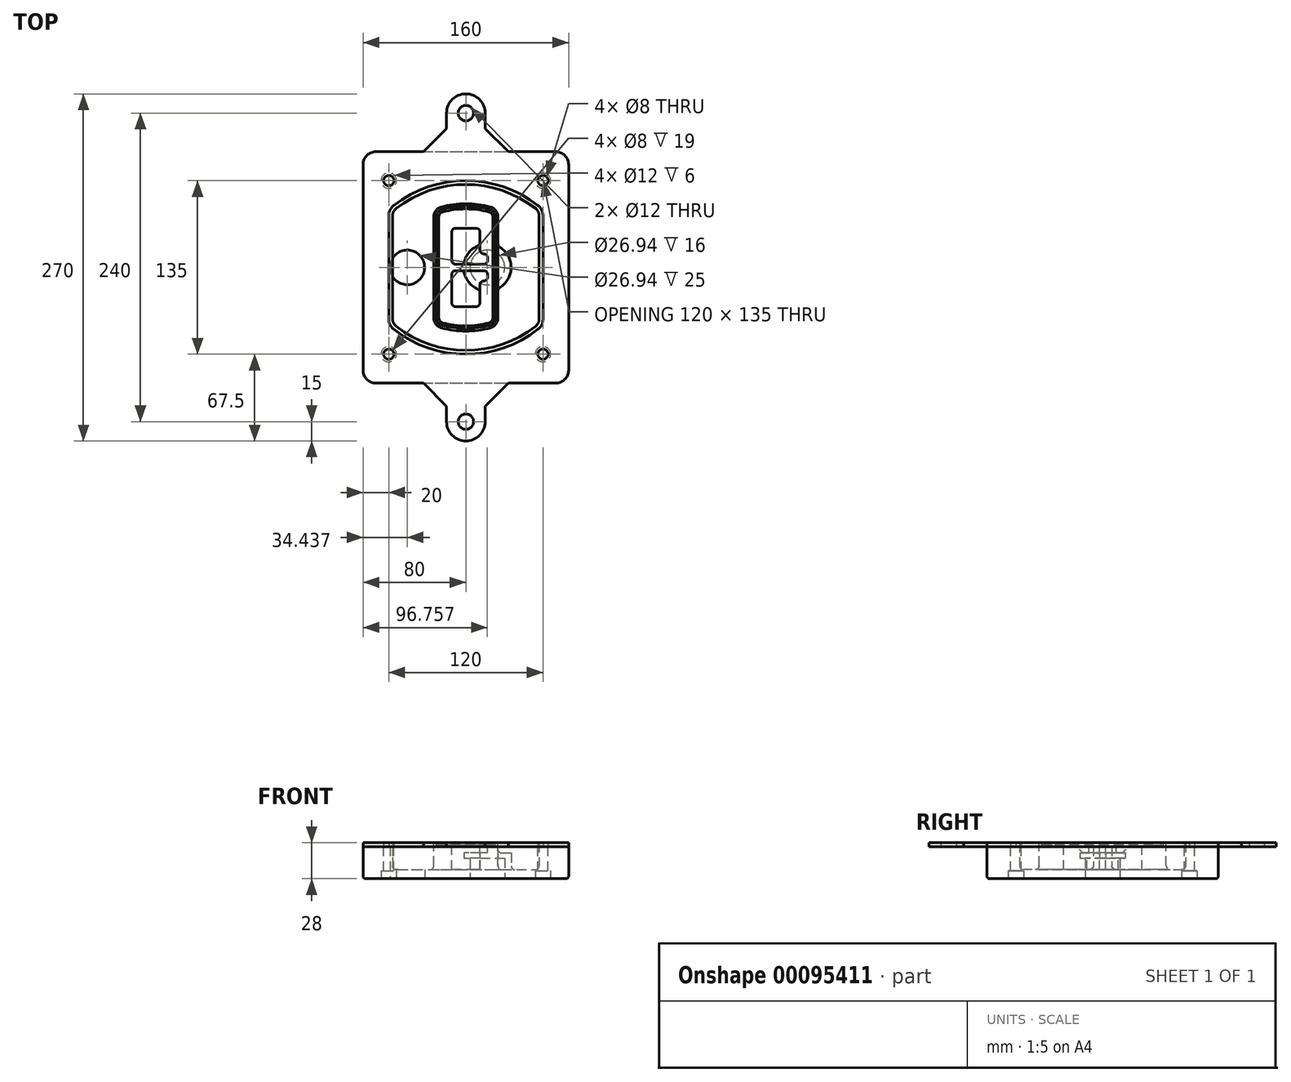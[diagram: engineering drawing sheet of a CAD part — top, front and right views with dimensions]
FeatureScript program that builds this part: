
annotation { "Feature Type Name" : "Feature", "Feature Type Description" : "" }
export const myFeature = defineFeature(function(context is Context, id is Id, definition is map)
    precondition{}
    {
        {
            var Q0;
            Q0=qCreatedBy(makeId("Top.planeOp"),FACE);
            var sketch = newSketch(context, id + "F0", { "sketchPlane" : qUnion([Q0])});
            skPoint(sketch, "E0.rect.middle", {"position": v(0, 0) * mm});
            skLineSegment(sketch, "E1.bottom", {"start": v(-70, -90) * mm, "end": v(70, -90) * mm});
            skLineSegment(sketch, "E1.top", {"start": v(-70, 90) * mm, "end": v(70, 90) * mm});
            skLineSegment(sketch, "E1.left", {"start": v(-80, -80) * mm, "end": v(-80, 80) * mm});
            skLineSegment(sketch, "E1.right", {"start": v(80, -80) * mm, "end": v(80, 80) * mm});
            skLineSegment(sketch, "E2", {"start": v(-80, 90) * mm, "end": v(80, -90) * mm, "construction": true});
            skLineSegment(sketch, "E3", {"start": v(80, 90) * mm, "end": v(-80, -90) * mm, "construction": true});
            skCircle(sketch, "E4", {"center": v(-60, 67.5) * mm, "radius": 4 * mm});
            skCircle(sketch, "E5", {"center": v(60, 67.5) * mm, "radius": 4 * mm});
            skCircle(sketch, "E6", {"center": v(60, -67.5) * mm, "radius": 4 * mm});
            skCircle(sketch, "E7", {"center": v(-60, -67.5) * mm, "radius": 4 * mm});
            skLineSegment(sketch, "E8", {"start": v(-60, 67.5) * mm, "end": v(60, 67.5) * mm, "construction": true});
            skLineSegment(sketch, "E9", {"start": v(60, 67.5) * mm, "end": v(60, -67.5) * mm, "construction": true});
            skLineSegment(sketch, "E10", {"start": v(60, -67.5) * mm, "end": v(-60, -67.5) * mm, "construction": true});
            skLineSegment(sketch, "E11", {"start": v(-60, -67.5) * mm, "end": v(-60, 67.5) * mm, "construction": true});
            skLineSegment(sketch, "E12", {"start": v(-60, 40.3) * mm, "end": v(-60, -40.3) * mm});
            skLineSegment(sketch, "E13", {"start": v(60, 40.3) * mm, "end": v(60, -40.3) * mm});
            skArc(sketch, "E14", {"start": v(56.15, 48.18) * mm, "mid": v(0, 67.5) * mm, "end": v(-56.15, 48.18) * mm});
            skArc(sketch, "E15", {"start": v(-56.15, -48.18) * mm, "mid": v(0, -67.5) * mm, "end": v(56.15, -48.18) * mm});
            skLineSegment(sketch, "E16", {"start": v(-60, 0) * mm, "end": v(60, 0) * mm, "construction": true});
            skPoint(sketch, "E17.visualSharp", {"position": v(-60, -45) * mm});
            skArc(sketch, "E17.filletArc", {"start": v(-60, -40.3) * mm, "mid": v(-58.99, -44.68) * mm, "end": v(-56.15, -48.18) * mm});
            skPoint(sketch, "E18.visualSharp", {"position": v(-60, 45) * mm});
            skArc(sketch, "E18.filletArc", {"start": v(-56.15, 48.18) * mm, "mid": v(-58.99, 44.68) * mm, "end": v(-60, 40.3) * mm});
            skPoint(sketch, "E19.visualSharp", {"position": v(60, 45) * mm});
            skArc(sketch, "E19.filletArc", {"start": v(60, 40.3) * mm, "mid": v(58.99, 44.68) * mm, "end": v(56.15, 48.18) * mm});
            skPoint(sketch, "E20.visualSharp", {"position": v(60, -45) * mm});
            skArc(sketch, "E20.filletArc", {"start": v(56.15, -48.18) * mm, "mid": v(58.99, -44.68) * mm, "end": v(60, -40.3) * mm});
            skPoint(sketch, "E21.visualSharp", {"position": v(-80, 90) * mm});
            skArc(sketch, "E21.filletArc", {"start": v(-70, 90) * mm, "mid": v(-77.07, 87.07) * mm, "end": v(-80, 80) * mm});
            skPoint(sketch, "E22.visualSharp", {"position": v(80, 90) * mm});
            skArc(sketch, "E22.filletArc", {"start": v(80, 80) * mm, "mid": v(77.07, 87.07) * mm, "end": v(70, 90) * mm});
            skPoint(sketch, "E23.visualSharp", {"position": v(80, -90) * mm});
            skArc(sketch, "E23.filletArc", {"start": v(70, -90) * mm, "mid": v(77.07, -87.07) * mm, "end": v(80, -80) * mm});
            skPoint(sketch, "E24.visualSharp", {"position": v(-80, -90) * mm});
            skArc(sketch, "E24.filletArc", {"start": v(-80, -80) * mm, "mid": v(-77.07, -87.07) * mm, "end": v(-70, -90) * mm});
            skArc(sketch, "E25.0", {"start": v(57, 40.3) * mm, "mid": v(56.3, 43.36) * mm, "end": v(54.3, 45.81) * mm});
            skLineSegment(sketch, "E25.1", {"start": v(57, 40.3) * mm, "end": v(57, -40.3) * mm});
            skArc(sketch, "E25.2", {"start": v(54.3, -45.81) * mm, "mid": v(56.3, -43.36) * mm, "end": v(57, -40.3) * mm});
            skArc(sketch, "E25.3", {"start": v(-54.3, -45.81) * mm, "mid": v(0, -64.5) * mm, "end": v(54.3, -45.81) * mm});
            skArc(sketch, "E25.4", {"start": v(-57, -40.3) * mm, "mid": v(-56.3, -43.36) * mm, "end": v(-54.3, -45.81) * mm});
            skArc(sketch, "E25.5", {"start": v(54.3, 45.81) * mm, "mid": v(0, 64.5) * mm, "end": v(-54.3, 45.81) * mm});
            skLineSegment(sketch, "E25.6", {"start": v(-57, 40.3) * mm, "end": v(-57, -40.3) * mm});
            skArc(sketch, "E25.7", {"start": v(-54.3, 45.81) * mm, "mid": v(-56.3, 43.36) * mm, "end": v(-57, 40.3) * mm});
            skArc(sketch, "E26.0", {"start": v(-58.62, 51.33) * mm, "mid": v(-62.58, 46.43) * mm, "end": v(-64, 40.3) * mm});
            skArc(sketch, "E26.1", {"start": v(58.62, 51.33) * mm, "mid": v(0, 71.5) * mm, "end": v(-58.62, 51.33) * mm});
            skArc(sketch, "E26.2", {"start": v(64, 40.3) * mm, "mid": v(62.58, 46.43) * mm, "end": v(58.62, 51.33) * mm});
            skLineSegment(sketch, "E26.3", {"start": v(64, 40.3) * mm, "end": v(64, -40.3) * mm});
            skArc(sketch, "E26.4", {"start": v(58.62, -51.33) * mm, "mid": v(62.58, -46.43) * mm, "end": v(64, -40.3) * mm});
            skLineSegment(sketch, "E26.5", {"start": v(-64, 40.3) * mm, "end": v(-64, -40.3) * mm});
            skArc(sketch, "E26.6", {"start": v(-58.62, -51.33) * mm, "mid": v(0, -71.5) * mm, "end": v(58.62, -51.33) * mm});
            skArc(sketch, "E26.7", {"start": v(-64, -40.3) * mm, "mid": v(-62.58, -46.43) * mm, "end": v(-58.62, -51.33) * mm});
            skSolve(sketch);
        }
        {
            var Q0;
            Q0=makeQuery(id+"F0.imprint","IMPRINT",FACE,{"disambiguationData":[TD([[makeQuery(id+"F0.imprint","IMPRINT",EDGE,{"derivedFrom":sQuery(id+"F0.wireOp",EDGE,"E1.bottom")}),1.0]])]});
            var Q1;
            Q1=makeQuery(id+"F0.imprint","IMPRINT",FACE,{"disambiguationData":[TD([[makeQuery(id+"F0.imprint","IMPRINT",EDGE,{"derivedFrom":sQuery(id+"F0.wireOp",EDGE,"E12")}),1.0]])]});
            var Q2;
            Q2=makeQuery(id+"F0.imprint","IMPRINT",FACE,{"disambiguationData":[TD([[makeQuery(id+"F0.imprint","IMPRINT",EDGE,{"derivedFrom":sQuery(id+"F0.wireOp",EDGE,"E25.0")}),1.0]])]});
            var Q3;
            Q3=makeQuery(id+"F0.imprint","IMPRINT",FACE,{"disambiguationData":[TD([[makeQuery(id+"F0.imprint","IMPRINT",EDGE,{"derivedFrom":sQuery(id+"F0.wireOp",EDGE,"E12")}),-1.0]])]});
            extrude(context, id + "F1", {"entities" : qUnion([Q0, Q1, Q2, Q3]), "oppositeDirection" : true, "depth" : 25 * mm});
        }
        {
            var Q0;
            Q0=makeQuery(id+"F0.imprint","IMPRINT",FACE,{"disambiguationData":[TD([[makeQuery(id+"F0.imprint","IMPRINT",EDGE,{"derivedFrom":sQuery(id+"F0.wireOp",EDGE,"E12")}),1.0]])]});
            extrude(context, id + "F2", {"entities" : qUnion([Q0]), "operationType" : NewBodyOperationType.ADD, "depth" : 3 * mm});
        }
        {
            var Q0;
            Q0=makeQuery(id+"F0.imprint","IMPRINT",FACE,{"disambiguationData":[TD([[makeQuery(id+"F0.imprint","IMPRINT",EDGE,{"derivedFrom":sQuery(id+"F0.wireOp",EDGE,"E25.0")}),1.0]])]});
            extrude(context, id + "F3", {"entities" : qUnion([Q0]), "operationType" : NewBodyOperationType.REMOVE, "oppositeDirection" : true, "depth" : 18 * mm});
        }
        {
            var Q0;
            Q0=makeQuery(id+"F2.opExtrude","CAP_FACE",FACE,{"disambiguationData":[OSD([sQuery(id+"F0.wireOp",EDGE,"E12"),sQuery(id+"F0.wireOp",EDGE,"E13"),sQuery(id+"F0.wireOp",EDGE,"E14"),sQuery(id+"F0.wireOp",EDGE,"E15"),sQuery(id+"F0.wireOp",EDGE,"E17.filletArc"),sQuery(id+"F0.wireOp",EDGE,"E18.filletArc"),sQuery(id+"F0.wireOp",EDGE,"E19.filletArc"),sQuery(id+"F0.wireOp",EDGE,"E20.filletArc"),sQuery(id+"F0.wireOp",EDGE,"E25.0"),sQuery(id+"F0.wireOp",EDGE,"E25.1"),sQuery(id+"F0.wireOp",EDGE,"E25.2"),sQuery(id+"F0.wireOp",EDGE,"E25.3"),sQuery(id+"F0.wireOp",EDGE,"E25.4"),sQuery(id+"F0.wireOp",EDGE,"E25.5"),sQuery(id+"F0.wireOp",EDGE,"E25.6"),sQuery(id+"F0.wireOp",EDGE,"E25.7")])],"isStart":false});
            var sketch = newSketch(context, id + "F4", { "sketchPlane" : qUnion([Q0])});
            skArc(sketch, "E27.0", {"start": v(-19.08, -46.97) * mm, "mid": v(0, -49.5) * mm, "end": v(19.08, -46.97) * mm});
            skArc(sketch, "E28.0", {"start": v(19.08, 46.97) * mm, "mid": v(0, 49.5) * mm, "end": v(-19.08, 46.97) * mm});
            skLineSegment(sketch, "E29", {"start": v(-25, 39.25) * mm, "end": v(-25, -39.25) * mm});
            skLineSegment(sketch, "E30", {"start": v(25, 39.25) * mm, "end": v(25, -39.25) * mm});
            skLineSegment(sketch, "E31", {"start": v(-25, 45.1) * mm, "end": v(25, 45.1) * mm, "construction": true});
            skLineSegment(sketch, "E32", {"start": v(-25, -45.1) * mm, "end": v(25, -45.1) * mm, "construction": true});
            skPoint(sketch, "E33.visualSharp", {"position": v(-25, 45.1) * mm});
            skArc(sketch, "E33.filletArc", {"start": v(-19.08, 46.97) * mm, "mid": v(-23.35, 44.11) * mm, "end": v(-25, 39.25) * mm});
            skPoint(sketch, "E34.visualSharp", {"position": v(25, 45.1) * mm});
            skArc(sketch, "E34.filletArc", {"start": v(25, 39.25) * mm, "mid": v(23.35, 44.11) * mm, "end": v(19.08, 46.97) * mm});
            skPoint(sketch, "E35.visualSharp", {"position": v(25, -45.1) * mm});
            skArc(sketch, "E35.filletArc", {"start": v(19.08, -46.97) * mm, "mid": v(23.35, -44.11) * mm, "end": v(25, -39.25) * mm});
            skPoint(sketch, "E36.visualSharp", {"position": v(-25, -45.1) * mm});
            skArc(sketch, "E36.filletArc", {"start": v(-25, -39.25) * mm, "mid": v(-23.35, -44.11) * mm, "end": v(-19.08, -46.97) * mm});
            skArc(sketch, "E37.0", {"start": v(54.3, 45.81) * mm, "mid": v(0, 64.5) * mm, "end": v(-54.3, 45.81) * mm});
            skArc(sketch, "E37.1", {"start": v(-54.3, 45.81) * mm, "mid": v(-56.3, 43.36) * mm, "end": v(-57, 40.3) * mm});
            skLineSegment(sketch, "E37.2", {"start": v(-57, 40.3) * mm, "end": v(-57, -40.3) * mm});
            skArc(sketch, "E37.3", {"start": v(-57, -40.3) * mm, "mid": v(-56.3, -43.36) * mm, "end": v(-54.3, -45.81) * mm});
            skArc(sketch, "E37.4", {"start": v(-54.3, -45.81) * mm, "mid": v(0, -64.5) * mm, "end": v(54.3, -45.81) * mm});
            skArc(sketch, "E37.5", {"start": v(54.3, -45.81) * mm, "mid": v(56.3, -43.36) * mm, "end": v(57, -40.3) * mm});
            skLineSegment(sketch, "E37.6", {"start": v(57, 40.3) * mm, "end": v(57, -40.3) * mm});
            skArc(sketch, "E37.7", {"start": v(57, 40.3) * mm, "mid": v(56.3, 43.36) * mm, "end": v(54.3, 45.81) * mm});
            skLineSegment(sketch, "E38.0", {"start": v(23, 39.25) * mm, "end": v(23, -39.25) * mm});
            skArc(sketch, "E38.1", {"start": v(18.56, -45.04) * mm, "mid": v(21.76, -42.9) * mm, "end": v(23, -39.25) * mm});
            skArc(sketch, "E38.2", {"start": v(-18.56, -45.04) * mm, "mid": v(0, -47.5) * mm, "end": v(18.56, -45.04) * mm});
            skArc(sketch, "E38.3", {"start": v(-23, -39.25) * mm, "mid": v(-21.76, -42.9) * mm, "end": v(-18.56, -45.04) * mm});
            skLineSegment(sketch, "E38.4", {"start": v(-23, 39.25) * mm, "end": v(-23, -39.25) * mm});
            skArc(sketch, "E38.5", {"start": v(23, 39.25) * mm, "mid": v(21.76, 42.9) * mm, "end": v(18.56, 45.04) * mm});
            skArc(sketch, "E38.6", {"start": v(-18.56, 45.04) * mm, "mid": v(-21.76, 42.9) * mm, "end": v(-23, 39.25) * mm});
            skArc(sketch, "E38.7", {"start": v(18.56, 45.04) * mm, "mid": v(0, 47.5) * mm, "end": v(-18.56, 45.04) * mm});
            skArc(sketch, "E39.0", {"start": v(21, 39.25) * mm, "mid": v(20.18, 41.68) * mm, "end": v(18.04, 43.1) * mm});
            skLineSegment(sketch, "E39.1", {"start": v(21, 39.25) * mm, "end": v(21, -39.25) * mm});
            skArc(sketch, "E39.2", {"start": v(18.04, -43.1) * mm, "mid": v(20.18, -41.68) * mm, "end": v(21, -39.25) * mm});
            skArc(sketch, "E39.3", {"start": v(-18.04, -43.1) * mm, "mid": v(0, -45.5) * mm, "end": v(18.04, -43.1) * mm});
            skArc(sketch, "E39.4", {"start": v(-21, -39.25) * mm, "mid": v(-20.18, -41.68) * mm, "end": v(-18.04, -43.1) * mm});
            skArc(sketch, "E39.5", {"start": v(18.04, 43.1) * mm, "mid": v(0, 45.5) * mm, "end": v(-18.04, 43.1) * mm});
            skLineSegment(sketch, "E39.6", {"start": v(-21, 39.25) * mm, "end": v(-21, -39.25) * mm});
            skArc(sketch, "E39.7", {"start": v(-18.04, 43.1) * mm, "mid": v(-20.18, 41.68) * mm, "end": v(-21, 39.25) * mm});
            skLineSegment(sketch, "E40", {"start": v(-25, 0) * mm, "end": v(25, 0) * mm, "construction": true});
            skLineSegment(sketch, "E41", {"start": v(-11, 5.5) * mm, "end": v(-11, 27.5) * mm});
            skLineSegment(sketch, "E42", {"start": v(-8, 30.5) * mm, "end": v(8, 30.5) * mm});
            skLineSegment(sketch, "E43", {"start": v(11, 27.5) * mm, "end": v(11, 13.5) * mm});
            skLineSegment(sketch, "E44", {"start": v(14, 10.5) * mm, "end": v(14, 10.5) * mm});
            skLineSegment(sketch, "E45", {"start": v(17, 7.5) * mm, "end": v(17, 5.5) * mm});
            skLineSegment(sketch, "E46", {"start": v(14, 2.5) * mm, "end": v(-8, 2.5) * mm});
            skPoint(sketch, "E47.visualSharp", {"position": v(-11, 30.5) * mm});
            skArc(sketch, "E47.filletArc", {"start": v(-8, 30.5) * mm, "mid": v(-10.12, 29.62) * mm, "end": v(-11, 27.5) * mm});
            skPoint(sketch, "E48.visualSharp", {"position": v(11, 30.5) * mm});
            skArc(sketch, "E48.filletArc", {"start": v(11, 27.5) * mm, "mid": v(10.12, 29.62) * mm, "end": v(8, 30.5) * mm});
            skPoint(sketch, "E49.visualSharp", {"position": v(11, 10.5) * mm});
            skArc(sketch, "E49.filletArc", {"start": v(11, 13.5) * mm, "mid": v(11.88, 11.38) * mm, "end": v(14, 10.5) * mm});
            skPoint(sketch, "E50.visualSharp", {"position": v(17, 10.5) * mm});
            skArc(sketch, "E50.filletArc", {"start": v(17, 7.5) * mm, "mid": v(16.12, 9.62) * mm, "end": v(14, 10.5) * mm});
            skPoint(sketch, "E51.visualSharp", {"position": v(17, 2.5) * mm});
            skArc(sketch, "E51.filletArc", {"start": v(14, 2.5) * mm, "mid": v(16.12, 3.38) * mm, "end": v(17, 5.5) * mm});
            skPoint(sketch, "E52.visualSharp", {"position": v(-11, 2.5) * mm});
            skArc(sketch, "E52.filletArc", {"start": v(-11, 5.5) * mm, "mid": v(-10.12, 3.38) * mm, "end": v(-8, 2.5) * mm});
            skLineSegment(sketch, "E53.0.MirrorCS", {"start": v(14, -2.5) * mm, "end": v(-8, -2.5) * mm});
            skArc(sketch, "E54.0.MirrorCS", {"start": v(-11, -5.5) * mm, "mid": v(-10.12, -3.38) * mm, "end": v(-8, -2.5) * mm});
            skLineSegment(sketch, "E55.0.MirrorCS", {"start": v(-11, -5.5) * mm, "end": v(-11, -27.5) * mm});
            skArc(sketch, "E56.0.MirrorCS", {"start": v(-8, -30.5) * mm, "mid": v(-10.12, -29.62) * mm, "end": v(-11, -27.5) * mm});
            skLineSegment(sketch, "E57.0.MirrorCS", {"start": v(-8, -30.5) * mm, "end": v(8, -30.5) * mm});
            skArc(sketch, "E58.0.MirrorCS", {"start": v(11, -27.5) * mm, "mid": v(10.12, -29.62) * mm, "end": v(8, -30.5) * mm});
            skLineSegment(sketch, "E59.0.MirrorCS", {"start": v(11, -27.5) * mm, "end": v(11, -13.5) * mm});
            skArc(sketch, "E60.0.MirrorCS", {"start": v(11, -13.5) * mm, "mid": v(11.88, -11.38) * mm, "end": v(14, -10.5) * mm});
            skArc(sketch, "E61.0.MirrorCS", {"start": v(17, -7.5) * mm, "mid": v(16.12, -9.62) * mm, "end": v(14, -10.5) * mm});
            skLineSegment(sketch, "E62.0.MirrorCS", {"start": v(17, -7.5) * mm, "end": v(17, -5.5) * mm});
            skArc(sketch, "E63.0.MirrorCS", {"start": v(14, -2.5) * mm, "mid": v(16.12, -3.38) * mm, "end": v(17, -5.5) * mm});
            skSolve(sketch);
        }
        {
            var Q0;
            Q0=makeQuery(id+"F4.imprint","IMPRINT",FACE,{"disambiguationData":[TD([[makeQuery(id+"F4.imprint","IMPRINT",EDGE,{"derivedFrom":sQuery(id+"F4.wireOp",EDGE,"E27.0")}),1.0]])]});
            var Q1;
            Q1=makeQuery(id+"F4.imprint","IMPRINT",FACE,{"disambiguationData":[TD([[makeQuery(id+"F4.imprint","IMPRINT",EDGE,{"derivedFrom":sQuery(id+"F4.wireOp",EDGE,"E38.0")}),-1.0]])]});
            var Q2;
            Q2=makeQuery(id+"F4.imprint","IMPRINT",FACE,{"disambiguationData":[TD([[makeQuery(id+"F4.imprint","IMPRINT",EDGE,{"derivedFrom":sQuery(id+"F4.wireOp",EDGE,"E39.0")}),1.0]])]});
            extrude(context, id + "F5", {"entities" : qUnion([Q0, Q1, Q2]), "operationType" : NewBodyOperationType.ADD, "endBound" : BoundingType.UP_TO_NEXT, "oppositeDirection" : true, "depth" : 25 * mm});
        }
        {
            var Q0;
            Q0=makeQuery(id+"F4.imprint","IMPRINT",FACE,{"disambiguationData":[TD([[makeQuery(id+"F4.imprint","IMPRINT",EDGE,{"derivedFrom":sQuery(id+"F4.wireOp",EDGE,"E38.0")}),-1.0]])]});
            extrude(context, id + "F6", {"entities" : qUnion([Q0]), "operationType" : NewBodyOperationType.REMOVE, "oppositeDirection" : true, "depth" : 2 * mm});
        }
        {
            var Q0;
            Q0=makeQuery(id+"F1.opExtrude","CAP_FACE",FACE,{"disambiguationData":[OSD([sQuery(id+"F0.wireOp",EDGE,"E1.bottom"),sQuery(id+"F0.wireOp",EDGE,"E1.top"),sQuery(id+"F0.wireOp",EDGE,"E1.left"),sQuery(id+"F0.wireOp",EDGE,"E1.right"),sQuery(id+"F0.wireOp",EDGE,"E4"),sQuery(id+"F0.wireOp",EDGE,"E5"),sQuery(id+"F0.wireOp",EDGE,"E6"),sQuery(id+"F0.wireOp",EDGE,"E7"),sQuery(id+"F0.wireOp",EDGE,"E21.filletArc"),sQuery(id+"F0.wireOp",EDGE,"E22.filletArc"),sQuery(id+"F0.wireOp",EDGE,"E23.filletArc"),sQuery(id+"F0.wireOp",EDGE,"E24.filletArc")])],"isStart":false});
            var sketch = newSketch(context, id + "F7", { "sketchPlane" : qUnion([Q0])});
            skCircle(sketch, "E64", {"center": v(16.76, 0) * mm, "radius": 13.47 * mm});
            skCircle(sketch, "E65", {"center": v(-45.56, 0) * mm, "radius": 13.47 * mm});
            skLineSegment(sketch, "E66", {"start": v(80, 0) * mm, "end": v(-80, 0) * mm});
            skCircle(sketch, "E67", {"center": v(16.76, 0) * mm, "radius": 18.47 * mm});
            skCircle(sketch, "E68", {"center": v(60, -67.5) * mm, "radius": 6 * mm});
            skCircle(sketch, "E69", {"center": v(-60, -67.5) * mm, "radius": 6 * mm});
            skCircle(sketch, "E70", {"center": v(-60, 67.5) * mm, "radius": 6 * mm});
            skCircle(sketch, "E71", {"center": v(60, 67.5) * mm, "radius": 6 * mm});
            skSolve(sketch);
        }
        {
            var Q0;
            {var subQ1=sQuery(id+"F7.wireOp",EDGE,"E66");var subQ4=sQuery(id+"F7.wireOp",EDGE,"E64");var subQ6=makeQuery(id+"F7.imprint","INTERSECT",VERTEX,{"disambiguationData":[OD(0.0)],"derivedFrom":[subQ4,subQ1]});Q0=makeQuery(id+"F7.imprint","IMPRINT",FACE,{"disambiguationData":[TD([[makeQuery(id+"F7.imprint","IMPRINT",EDGE,{"disambiguationData":[TD([[subQ6,-1.0]])],"derivedFrom":subQ4}),-1.0]])]});}
            var Q1;
            {var subQ0=sQuery(id+"F7.wireOp",EDGE,"E66");var subQ1=sQuery(id+"F7.wireOp",EDGE,"E64");var subQ3=makeQuery(id+"F7.imprint","INTERSECT",VERTEX,{"disambiguationData":[OD(0.0)],"derivedFrom":[subQ1,subQ0]});Q1=makeQuery(id+"F7.imprint","IMPRINT",FACE,{"disambiguationData":[TD([[makeQuery(id+"F7.imprint","IMPRINT",EDGE,{"disambiguationData":[TD([[subQ3,-1.0]])],"derivedFrom":subQ1}),1.0]])]});}
            var Q2;
            {var subQ0=sQuery(id+"F7.wireOp",EDGE,"E66");var subQ1=sQuery(id+"F7.wireOp",EDGE,"E64");var subQ3=makeQuery(id+"F7.imprint","INTERSECT",VERTEX,{"disambiguationData":[OD(0.0)],"derivedFrom":[subQ1,subQ0]});Q2=makeQuery(id+"F7.imprint","IMPRINT",FACE,{"disambiguationData":[TD([[makeQuery(id+"F7.imprint","IMPRINT",EDGE,{"disambiguationData":[TD([[subQ3,1.0]])],"derivedFrom":subQ1}),1.0]])]});}
            var Q3;
            {var subQ1=sQuery(id+"F7.wireOp",EDGE,"E66");var subQ4=sQuery(id+"F7.wireOp",EDGE,"E64");var subQ6=makeQuery(id+"F7.imprint","INTERSECT",VERTEX,{"disambiguationData":[OD(0.0)],"derivedFrom":[subQ4,subQ1]});Q3=makeQuery(id+"F7.imprint","IMPRINT",FACE,{"disambiguationData":[TD([[makeQuery(id+"F7.imprint","IMPRINT",EDGE,{"disambiguationData":[TD([[subQ6,1.0]])],"derivedFrom":subQ4}),-1.0]])]});}
            extrude(context, id + "F8", {"entities" : qUnion([Q0, Q1, Q2, Q3]), "operationType" : NewBodyOperationType.ADD, "oppositeDirection" : true, "depth" : 20 * mm});
        }
        {
            var Q0;
            {var subQ0=sQuery(id+"F7.wireOp",EDGE,"E66");var subQ1=sQuery(id+"F7.wireOp",EDGE,"E64");var subQ3=makeQuery(id+"F7.imprint","INTERSECT",VERTEX,{"disambiguationData":[OD(0.0)],"derivedFrom":[subQ1,subQ0]});Q0=makeQuery(id+"F7.imprint","IMPRINT",FACE,{"disambiguationData":[TD([[makeQuery(id+"F7.imprint","IMPRINT",EDGE,{"disambiguationData":[TD([[subQ3,-1.0]])],"derivedFrom":subQ1}),1.0]])]});}
            var Q1;
            {var subQ0=sQuery(id+"F7.wireOp",EDGE,"E66");var subQ1=sQuery(id+"F7.wireOp",EDGE,"E64");var subQ3=makeQuery(id+"F7.imprint","INTERSECT",VERTEX,{"disambiguationData":[OD(0.0)],"derivedFrom":[subQ1,subQ0]});Q1=makeQuery(id+"F7.imprint","IMPRINT",FACE,{"disambiguationData":[TD([[makeQuery(id+"F7.imprint","IMPRINT",EDGE,{"disambiguationData":[TD([[subQ3,1.0]])],"derivedFrom":subQ1}),1.0]])]});}
            extrude(context, id + "F9", {"entities" : qUnion([Q0, Q1]), "operationType" : NewBodyOperationType.REMOVE, "oppositeDirection" : true, "depth" : 16 * mm});
        }
        {
            var Q0;
            {var subQ0=sQuery(id+"F7.wireOp",EDGE,"E66");var subQ1=sQuery(id+"F7.wireOp",EDGE,"E65");var subQ3=makeQuery(id+"F7.imprint","INTERSECT",VERTEX,{"disambiguationData":[OD(0.0)],"derivedFrom":[subQ1,subQ0]});Q0=makeQuery(id+"F7.imprint","IMPRINT",FACE,{"disambiguationData":[TD([[makeQuery(id+"F7.imprint","IMPRINT",EDGE,{"disambiguationData":[TD([[subQ3,-1.0]])],"derivedFrom":subQ1}),1.0]])]});}
            var Q1;
            {var subQ0=sQuery(id+"F7.wireOp",EDGE,"E66");var subQ1=sQuery(id+"F7.wireOp",EDGE,"E65");var subQ3=makeQuery(id+"F7.imprint","INTERSECT",VERTEX,{"disambiguationData":[OD(0.0)],"derivedFrom":[subQ1,subQ0]});Q1=makeQuery(id+"F7.imprint","IMPRINT",FACE,{"disambiguationData":[TD([[makeQuery(id+"F7.imprint","IMPRINT",EDGE,{"disambiguationData":[TD([[subQ3,1.0]])],"derivedFrom":subQ1}),1.0]])]});}
            extrude(context, id + "F10", {"entities" : qUnion([Q0, Q1]), "operationType" : NewBodyOperationType.REMOVE, "oppositeDirection" : true, "depth" : 25 * mm});
        }
        {
            var Q0;
            Q0=makeQuery(id+"F7.imprint","IMPRINT",FACE,{"disambiguationData":[TD([[makeQuery(id+"F7.imprint","IMPRINT",EDGE,{"derivedFrom":sQuery(id+"F7.wireOp",EDGE,"E68")}),1.0]])]});
            var Q1;
            Q1=makeQuery(id+"F7.imprint","IMPRINT",FACE,{"disambiguationData":[TD([[makeQuery(id+"F7.imprint","IMPRINT",EDGE,{"derivedFrom":makeQuery(id+"F1.opExtrude","CAP_EDGE",EDGE,{"disambiguationData":[OSD([sQuery(id+"F0.wireOp",EDGE,"E5")])],"isStart":false})}),-1.0]])]});
            var Q2;
            Q2=makeQuery(id+"F7.imprint","IMPRINT",FACE,{"disambiguationData":[TD([[makeQuery(id+"F7.imprint","IMPRINT",EDGE,{"derivedFrom":sQuery(id+"F7.wireOp",EDGE,"E69")}),1.0]])]});
            var Q3;
            Q3=makeQuery(id+"F7.imprint","IMPRINT",FACE,{"disambiguationData":[TD([[makeQuery(id+"F7.imprint","IMPRINT",EDGE,{"derivedFrom":makeQuery(id+"F1.opExtrude","CAP_EDGE",EDGE,{"disambiguationData":[OSD([sQuery(id+"F0.wireOp",EDGE,"E4")])],"isStart":false})}),-1.0]])]});
            var Q4;
            Q4=makeQuery(id+"F7.imprint","IMPRINT",FACE,{"disambiguationData":[TD([[makeQuery(id+"F7.imprint","IMPRINT",EDGE,{"derivedFrom":sQuery(id+"F7.wireOp",EDGE,"E70")}),1.0]])]});
            var Q5;
            Q5=makeQuery(id+"F7.imprint","IMPRINT",FACE,{"disambiguationData":[TD([[makeQuery(id+"F7.imprint","IMPRINT",EDGE,{"derivedFrom":makeQuery(id+"F1.opExtrude","CAP_EDGE",EDGE,{"disambiguationData":[OSD([sQuery(id+"F0.wireOp",EDGE,"E7")])],"isStart":false})}),-1.0]])]});
            var Q6;
            Q6=makeQuery(id+"F7.imprint","IMPRINT",FACE,{"disambiguationData":[TD([[makeQuery(id+"F7.imprint","IMPRINT",EDGE,{"derivedFrom":sQuery(id+"F7.wireOp",EDGE,"E71")}),1.0]])]});
            var Q7;
            Q7=makeQuery(id+"F7.imprint","IMPRINT",FACE,{"disambiguationData":[TD([[makeQuery(id+"F7.imprint","IMPRINT",EDGE,{"derivedFrom":makeQuery(id+"F1.opExtrude","CAP_EDGE",EDGE,{"disambiguationData":[OSD([sQuery(id+"F0.wireOp",EDGE,"E6")])],"isStart":false})}),-1.0]])]});
            extrude(context, id + "F11", {"entities" : qUnion([Q0, Q1, Q2, Q3, Q4, Q5, Q6, Q7]), "operationType" : NewBodyOperationType.REMOVE, "oppositeDirection" : true, "depth" : 6 * mm});
        }
        {
            var Q0;
            Q0=makeQuery(id+"F9.boolean.opBoolean","COPY",FACE,{"derivedFrom":makeQuery(id+"F9.opExtrude","CAP_FACE",FACE,{"disambiguationData":[OSD([sQuery(id+"F7.wireOp",EDGE,"E64")])],"isStart":false})});
            var sketch = newSketch(context, id + "F12", { "sketchPlane" : qUnion([Q0])});
            skArc(sketch, "E72.0", {"start": v(11, 17.55) * mm, "mid": v(2.57, 11.82) * mm, "end": v(-1.54, 2.5) * mm});
            skArc(sketch, "E72.1", {"start": v(-1.54, -2.5) * mm, "mid": v(2.57, -11.82) * mm, "end": v(11, -17.55) * mm});
            skLineSegment(sketch, "E73", {"start": v(-1.54, -2.5) * mm, "end": v(14, -2.5) * mm});
            skLineSegment(sketch, "E74.0", {"start": v(14, 2.5) * mm, "end": v(-1.54, 2.5) * mm});
            skArc(sketch, "E74.1", {"start": v(14, 2.5) * mm, "mid": v(16.12, 3.38) * mm, "end": v(17, 5.5) * mm});
            skLineSegment(sketch, "E74.2", {"start": v(17, 7.5) * mm, "end": v(17, 5.5) * mm});
            skArc(sketch, "E74.3", {"start": v(17, 7.5) * mm, "mid": v(16.12, 9.62) * mm, "end": v(14, 10.5) * mm});
            skArc(sketch, "E74.4", {"start": v(11, 13.5) * mm, "mid": v(11.88, 11.38) * mm, "end": v(14, 10.5) * mm});
            skLineSegment(sketch, "E74.5", {"start": v(11, 17.55) * mm, "end": v(11, 13.5) * mm});
            skLineSegment(sketch, "E74.7", {"start": v(14, -2.5) * mm, "end": v(-1.54, -2.5) * mm});
            skArc(sketch, "E74.8", {"start": v(14, -2.5) * mm, "mid": v(16.12, -3.38) * mm, "end": v(17, -5.5) * mm});
            skLineSegment(sketch, "E74.9", {"start": v(17, -7.5) * mm, "end": v(17, -5.5) * mm});
            skArc(sketch, "E74.10", {"start": v(17, -7.5) * mm, "mid": v(16.12, -9.62) * mm, "end": v(14, -10.5) * mm});
            skArc(sketch, "E74.11", {"start": v(11, -13.5) * mm, "mid": v(11.88, -11.38) * mm, "end": v(14, -10.5) * mm});
            skLineSegment(sketch, "E74.12", {"start": v(11, -17.55) * mm, "end": v(11, -13.5) * mm});
            skPoint(sketch, "E75.orphan", {"position": v(11, -27.5) * mm});
            skPoint(sketch, "E76.orphan", {"position": v(-8, -2.5) * mm});
            skPoint(sketch, "E77.orphan", {"position": v(-8, 2.5) * mm});
            skPoint(sketch, "E78.orphan", {"position": v(11, 27.5) * mm});
            skSolve(sketch);
        }
        {
            var Q0;
            {var subQ7=sQuery(id+"F12.wireOp",EDGE,"E72.0");var subQ14=sQuery(id+"F12.wireOp",EDGE,"E72.1");var subQ16=sQuery(id+"F12.wireOp",EDGE,"E74.1");var subQ18=sQuery(id+"F12.wireOp",EDGE,"E74.8");Q0=qUnion([makeQuery(id+"F12.imprint","IMPRINT",FACE,{"disambiguationData":[TD([[makeQuery(id+"F12.imprint","IMPRINT",EDGE,{"derivedFrom":subQ7}),1.0]])]}),makeQuery(id+"F12.imprint","IMPRINT",FACE,{"disambiguationData":[TD([[makeQuery(id+"F12.imprint","IMPRINT",EDGE,{"derivedFrom":subQ14}),1.0]])]}),makeQuery(id+"F12.imprint","IMPRINT",FACE,{"disambiguationData":[TD([[makeQuery(id+"F12.imprint","IMPRINT",EDGE,{"derivedFrom":subQ16}),1.0]])]}),makeQuery(id+"F12.imprint","IMPRINT",FACE,{"disambiguationData":[TD([[makeQuery(id+"F12.imprint","IMPRINT",EDGE,{"derivedFrom":subQ18}),-1.0]])]})]);}
            var Q1;
            Q1=makeQuery(id+"F5.boolean.opBoolean","SPLIT",FACE,{"disambiguationData":[TD([makeQuery(id+"F5.opExtrude","SWEPT_FACE",FACE,{"disambiguationData":[OSD([sQuery(id+"F4.wireOp",EDGE,"E41")])]})])],"derivedFrom":makeQuery(id+"F3.boolean.opBoolean","COPY",FACE,{"derivedFrom":makeQuery(id+"F3.opExtrude","CAP_FACE",FACE,{"disambiguationData":[OSD([sQuery(id+"F0.wireOp",EDGE,"E25.0"),sQuery(id+"F0.wireOp",EDGE,"E25.1"),sQuery(id+"F0.wireOp",EDGE,"E25.2"),sQuery(id+"F0.wireOp",EDGE,"E25.3"),sQuery(id+"F0.wireOp",EDGE,"E25.4"),sQuery(id+"F0.wireOp",EDGE,"E25.5"),sQuery(id+"F0.wireOp",EDGE,"E25.6"),sQuery(id+"F0.wireOp",EDGE,"E25.7")])],"isStart":false})})});
            extrude(context, id + "F13", {"entities" : qUnion([Q0]), "operationType" : NewBodyOperationType.REMOVE, "endBound" : BoundingType.UP_TO_SURFACE, "endBoundEntityFace" : qUnion([Q1]), "depth" : 25 * mm});
        }
        {
            var Q0;
            Q0=makeQuery(id+"F3.boolean.opBoolean","COPY",EDGE,{"derivedFrom":makeQuery(id+"F3.opExtrude","CAP_EDGE",EDGE,{"disambiguationData":[OSD([sQuery(id+"F0.wireOp",EDGE,"E25.6")])],"isStart":false})});
            var Q1;
            Q1=makeQuery(id+"F8.boolean.opBoolean","INTERSECT",EDGE,{"derivedFrom":[makeQuery(id+"F5.opExtrude","SWEPT_FACE",FACE,{"disambiguationData":[OSD([sQuery(id+"F4.wireOp",EDGE,"E30")])]}),makeQuery(id+"F8.opExtrude","CAP_FACE",FACE,{"disambiguationData":[OSD([sQuery(id+"F7.wireOp",EDGE,"E67")])],"isStart":false})]});
            var Q2;
            Q2=makeQuery(id+"F8.boolean.opBoolean","INTERSECT",EDGE,{"disambiguationData":[OD(1.0)],"derivedFrom":[makeQuery(id+"F5.opExtrude","SWEPT_FACE",FACE,{"disambiguationData":[OSD([sQuery(id+"F4.wireOp",EDGE,"E30")])]}),makeQuery(id+"F8.opExtrude","SWEPT_FACE",FACE,{"disambiguationData":[OSD([sQuery(id+"F7.wireOp",EDGE,"E67")])]})]});
            var Q3;
            {var subQ0=sQuery(id+"F4.wireOp",EDGE,"E30");Q3=makeQuery(id+"F8.boolean.opBoolean","SPLIT",EDGE,{"disambiguationData":[TD([makeQuery(id+"F5.opExtrude","SWEPT_FACE",FACE,{"disambiguationData":[OSD([sQuery(id+"F4.wireOp",EDGE,"E35.filletArc")])]})])],"derivedFrom":makeQuery(id+"F5.opExtrude","CAP_EDGE",EDGE,{"disambiguationData":[OSD([subQ0])],"isStart":false})});}
            var Q4;
            {var subQ0=sQuery(id+"F0.wireOp",EDGE,"E25.7");var subQ1=sQuery(id+"F0.wireOp",EDGE,"E25.1");var subQ2=sQuery(id+"F0.wireOp",EDGE,"E25.6");var subQ3=sQuery(id+"F0.wireOp",EDGE,"E25.5");var subQ4=sQuery(id+"F0.wireOp",EDGE,"E25.4");var subQ5=sQuery(id+"F0.wireOp",EDGE,"E25.0");var subQ6=sQuery(id+"F0.wireOp",EDGE,"E25.2");var subQ7=sQuery(id+"F0.wireOp",EDGE,"E25.3");Q4=makeQuery(id+"F8.boolean.opBoolean","INTERSECT",EDGE,{"derivedFrom":[makeQuery(id+"F5.boolean.opBoolean","SPLIT",FACE,{"disambiguationData":[TD([makeQuery(id+"F2.opExtrude","SWEPT_FACE",FACE,{"disambiguationData":[OSD([subQ5])]})])],"derivedFrom":makeQuery(id+"F3.boolean.opBoolean","COPY",FACE,{"derivedFrom":makeQuery(id+"F3.opExtrude","CAP_FACE",FACE,{"disambiguationData":[OSD([subQ5,subQ1,subQ6,subQ7,subQ4,subQ3,subQ2,subQ0])],"isStart":false})})}),makeQuery(id+"F8.opExtrude","SWEPT_FACE",FACE,{"disambiguationData":[OSD([sQuery(id+"F7.wireOp",EDGE,"E67")])]})]});}
            var Q5;
            Q5=makeQuery(id+"F8.boolean.opBoolean","INTERSECT",EDGE,{"disambiguationData":[OD(0.0)],"derivedFrom":[makeQuery(id+"F5.opExtrude","SWEPT_FACE",FACE,{"disambiguationData":[OSD([sQuery(id+"F4.wireOp",EDGE,"E30")])]}),makeQuery(id+"F8.opExtrude","SWEPT_FACE",FACE,{"disambiguationData":[OSD([sQuery(id+"F7.wireOp",EDGE,"E67")])]})]});
            fillet(context, id + "F14", {"entities" : qUnion([Q0, Q1, Q2, Q3, Q4, Q5]), "radius" : 3 * mm, "tangentPropagation" : true, "allowEdgeOverflow" : false});
        }
        {
            var Q0;
            Q0=makeQuery(id+"F1.opExtrude","CAP_EDGE",EDGE,{"disambiguationData":[OSD([sQuery(id+"F0.wireOp",EDGE,"E1.bottom")])],"isStart":false});
            fillet(context, id + "F15", {"entities" : qUnion([Q0]), "radius" : 2 * mm, "tangentPropagation" : true, "allowEdgeOverflow" : false});
        }
        {
            var Q0;
            Q0=qCreatedBy(makeId("Top.planeOp"),FACE);
            var sketch = newSketch(context, id + "F16", { "sketchPlane" : qUnion([Q0])});
            skCircle(sketch, "E79", {"center": v(0, 120) * mm, "radius": 6 * mm});
            skLineSegment(sketch, "E80", {"start": v(-15, 120) * mm, "end": v(-15, 108) * mm});
            skLineSegment(sketch, "E81", {"start": v(15, 120) * mm, "end": v(15, 108) * mm});
            skLineSegment(sketch, "E82", {"start": v(0, 120) * mm, "end": v(0, 90) * mm, "construction": true});
            skArc(sketch, "E83", {"start": v(15, 120) * mm, "mid": v(0, 135) * mm, "end": v(-15, 120) * mm});
            skLineSegment(sketch, "E84", {"start": v(-15, 108) * mm, "end": v(-33, 90) * mm});
            skLineSegment(sketch, "E85", {"start": v(15, 108) * mm, "end": v(33, 90) * mm});
            skLineSegment(sketch, "E86.0", {"start": v(-70, 90) * mm, "end": v(70, 90) * mm});
            skArc(sketch, "E87.1", {"start": v(-70, 90) * mm, "mid": v(-77.07, 87.07) * mm, "end": v(-80, 80) * mm});
            skLineSegment(sketch, "E87.2", {"start": v(-80, -80) * mm, "end": v(-80, 80) * mm});
            skArc(sketch, "E87.3", {"start": v(-80, -80) * mm, "mid": v(-77.07, -87.07) * mm, "end": v(-70, -90) * mm});
            skLineSegment(sketch, "E87.4", {"start": v(-70, -90) * mm, "end": v(70, -90) * mm});
            skArc(sketch, "E87.5", {"start": v(70, -90) * mm, "mid": v(77.07, -87.07) * mm, "end": v(80, -80) * mm});
            skLineSegment(sketch, "E87.6", {"start": v(80, -80) * mm, "end": v(80, 80) * mm});
            skArc(sketch, "E87.7", {"start": v(80, 80) * mm, "mid": v(77.07, 87.07) * mm, "end": v(70, 90) * mm});
            skCircle(sketch, "E87.8", {"center": v(60, 67.5) * mm, "radius": 4 * mm});
            skCircle(sketch, "E87.9", {"center": v(-60, 67.5) * mm, "radius": 4 * mm});
            skCircle(sketch, "E87.10", {"center": v(-60, -67.5) * mm, "radius": 4 * mm});
            skCircle(sketch, "E87.11", {"center": v(60, -67.5) * mm, "radius": 4 * mm});
            skArc(sketch, "E87.12", {"start": v(-56.15, -48.18) * mm, "mid": v(0, -67.5) * mm, "end": v(56.15, -48.18) * mm});
            skArc(sketch, "E87.13", {"start": v(56.15, -48.18) * mm, "mid": v(58.99, -44.68) * mm, "end": v(60, -40.3) * mm});
            skLineSegment(sketch, "E87.14", {"start": v(60, 40.3) * mm, "end": v(60, -40.3) * mm});
            skArc(sketch, "E87.15", {"start": v(60, 40.3) * mm, "mid": v(58.99, 44.68) * mm, "end": v(56.15, 48.18) * mm});
            skArc(sketch, "E87.16", {"start": v(56.15, 48.18) * mm, "mid": v(0, 67.5) * mm, "end": v(-56.15, 48.18) * mm});
            skArc(sketch, "E87.17", {"start": v(-56.15, 48.18) * mm, "mid": v(-58.99, 44.68) * mm, "end": v(-60, 40.3) * mm});
            skLineSegment(sketch, "E87.18", {"start": v(-60, 40.3) * mm, "end": v(-60, -40.3) * mm});
            skArc(sketch, "E87.19", {"start": v(-60, -40.3) * mm, "mid": v(-58.99, -44.68) * mm, "end": v(-56.15, -48.18) * mm});
            skLineSegment(sketch, "E88", {"start": v(-80, 0) * mm, "end": v(80, 0) * mm, "construction": true});
            skArc(sketch, "E89.MirrorCS", {"start": v(-15, 120) * mm, "mid": v(0, 135) * mm, "end": v(15, 120) * mm});
            skLineSegment(sketch, "E90.MirrorCS", {"start": v(80, 0) * mm, "end": v(-80, 0) * mm, "construction": true});
            skArc(sketch, "E91.MirrorCS", {"start": v(-56.15, 48.18) * mm, "mid": v(0, 67.5) * mm, "end": v(56.15, 48.18) * mm});
            skLineSegment(sketch, "E92.MirrorCS", {"start": v(70, 90) * mm, "end": v(-70, 90) * mm});
            skLineSegment(sketch, "E93.MirrorCS", {"start": v(15, -108) * mm, "end": v(33, -90) * mm});
            skLineSegment(sketch, "E94.MirrorCS", {"start": v(15, -120) * mm, "end": v(15, -108) * mm});
            skArc(sketch, "E95.MirrorCS", {"start": v(-15, -120) * mm, "mid": v(0, -135) * mm, "end": v(15, -120) * mm});
            skLineSegment(sketch, "E96.MirrorCS", {"start": v(-15, -120) * mm, "end": v(-15, -108) * mm});
            skLineSegment(sketch, "E97.MirrorCS", {"start": v(-15, -108) * mm, "end": v(-33, -90) * mm});
            skCircle(sketch, "E98.MirrorC", {"center": v(0, -120) * mm, "radius": 6 * mm});
            skLineSegment(sketch, "E99.MirrorCS", {"start": v(0, -120) * mm, "end": v(0, -90) * mm, "construction": true});
            skSolve(sketch);
        }
        {
            var Q0;
            {var subQ0=sQuery(id+"F16.wireOp",EDGE,"E84");Q0=makeQuery(id+"F16.imprint","IMPRINT",FACE,{"disambiguationData":[TD([[makeQuery(id+"F16.imprint","IMPRINT",EDGE,{"derivedFrom":subQ0}),1.0]])]});}
            var Q1;
            {var subQ0=sQuery(id+"F16.wireOp",EDGE,"E93.MirrorCS");Q1=makeQuery(id+"F16.imprint","IMPRINT",FACE,{"disambiguationData":[TD([[makeQuery(id+"F16.imprint","IMPRINT",EDGE,{"derivedFrom":subQ0}),1.0]])]});}
            var Q2;
            {var subQ1=sQuery(id+"F16.wireOp",EDGE,"E87.1");Q2=makeQuery(id+"F16.imprint","IMPRINT",FACE,{"disambiguationData":[TD([[makeQuery(id+"F16.imprint","IMPRINT",EDGE,{"derivedFrom":subQ1}),1.0]])]});}
            var Q3;
            {var subQ0=sQuery(id+"F4.wireOp",EDGE,"E36.filletArc");var subQ1=sQuery(id+"F4.wireOp",EDGE,"E35.filletArc");var subQ2=sQuery(id+"F4.wireOp",EDGE,"E34.filletArc");var subQ3=sQuery(id+"F4.wireOp",EDGE,"E33.filletArc");var subQ4=sQuery(id+"F4.wireOp",EDGE,"E27.0");var subQ5=sQuery(id+"F4.wireOp",EDGE,"E30");var subQ6=sQuery(id+"F4.wireOp",EDGE,"E28.0");var subQ7=sQuery(id+"F4.wireOp",EDGE,"E29");Q3=makeQuery(id+"F6.boolean.opBoolean","SPLIT",FACE,{"disambiguationData":[TD([makeQuery(id+"F5.opExtrude","SWEPT_FACE",FACE,{"disambiguationData":[OSD([subQ4])]})])],"derivedFrom":makeQuery(id+"F5.opExtrude","CAP_FACE",FACE,{"disambiguationData":[OSD([subQ4,subQ6,subQ7,subQ5,subQ3,subQ2,subQ1,subQ0,sQuery(id+"F4.wireOp",EDGE,"E41"),sQuery(id+"F4.wireOp",EDGE,"E42"),sQuery(id+"F4.wireOp",EDGE,"E43"),sQuery(id+"F4.wireOp",EDGE,"E45"),sQuery(id+"F4.wireOp",EDGE,"E46"),sQuery(id+"F4.wireOp",EDGE,"E47.filletArc"),sQuery(id+"F4.wireOp",EDGE,"E48.filletArc"),sQuery(id+"F4.wireOp",EDGE,"E49.filletArc"),sQuery(id+"F4.wireOp",EDGE,"E50.filletArc"),sQuery(id+"F4.wireOp",EDGE,"E51.filletArc"),sQuery(id+"F4.wireOp",EDGE,"E52.filletArc"),sQuery(id+"F4.wireOp",EDGE,"E53.0.MirrorCS"),sQuery(id+"F4.wireOp",EDGE,"E54.0.MirrorCS"),sQuery(id+"F4.wireOp",EDGE,"E55.0.MirrorCS"),sQuery(id+"F4.wireOp",EDGE,"E56.0.MirrorCS"),sQuery(id+"F4.wireOp",EDGE,"E57.0.MirrorCS"),sQuery(id+"F4.wireOp",EDGE,"E58.0.MirrorCS"),sQuery(id+"F4.wireOp",EDGE,"E59.0.MirrorCS"),sQuery(id+"F4.wireOp",EDGE,"E60.0.MirrorCS"),sQuery(id+"F4.wireOp",EDGE,"E61.0.MirrorCS"),sQuery(id+"F4.wireOp",EDGE,"E62.0.MirrorCS"),sQuery(id+"F4.wireOp",EDGE,"E63.0.MirrorCS")])],"isStart":true})});}
            extrude(context, id + "F17", {"entities" : qUnion([Q0, Q1, Q2]), "endBound" : BoundingType.UP_TO_SURFACE, "endBoundEntityFace" : qUnion([Q3]), "depth" : 25 * mm});
        }
    });
